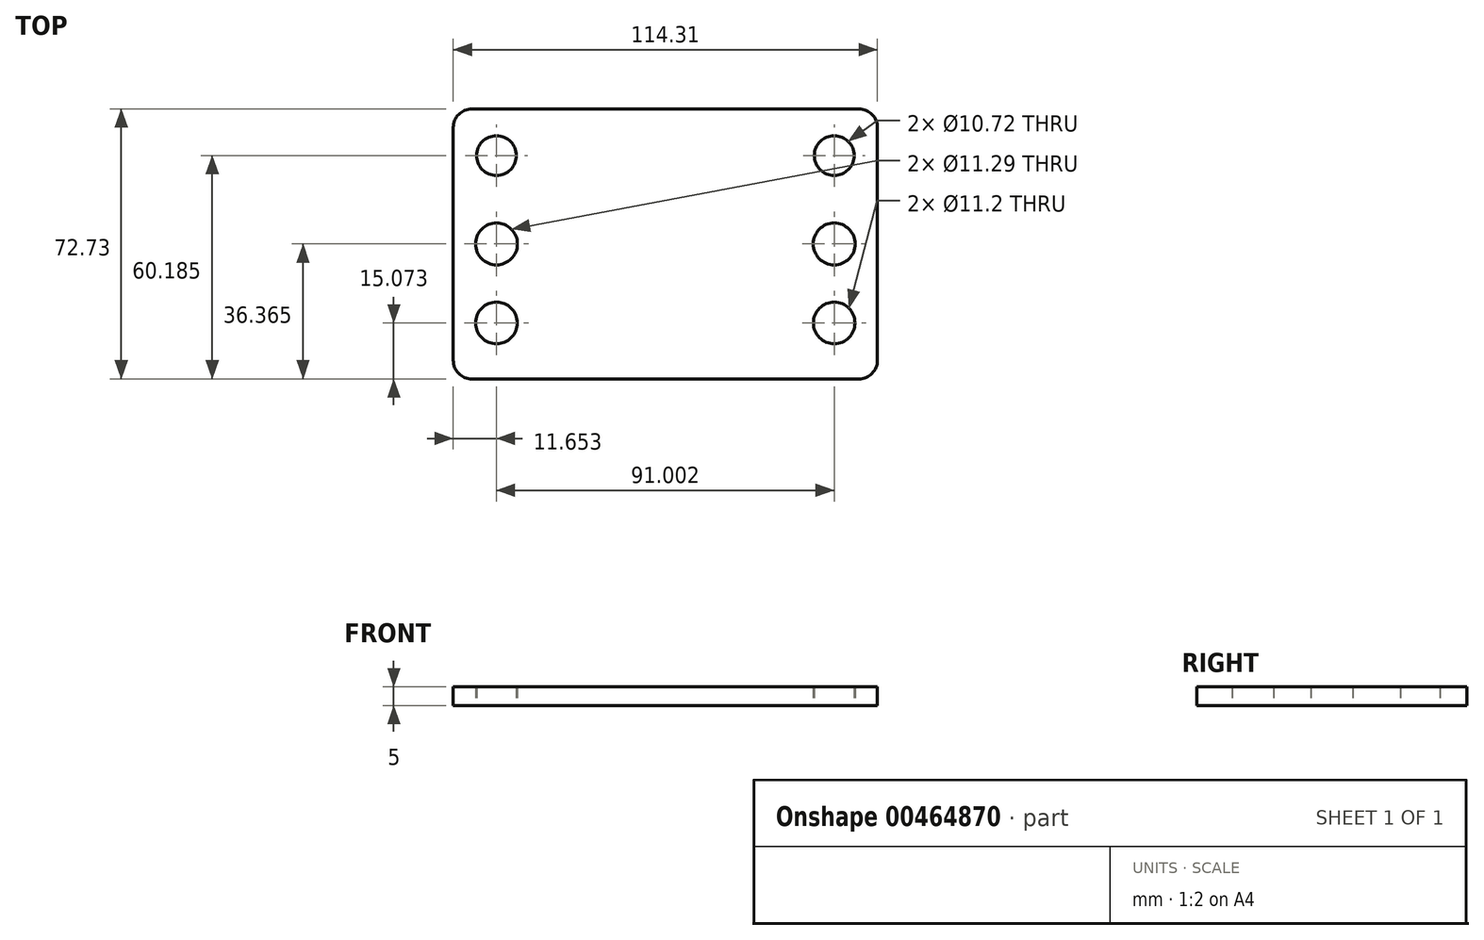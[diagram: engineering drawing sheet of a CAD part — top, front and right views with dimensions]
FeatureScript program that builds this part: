
annotation { "Feature Type Name" : "Feature", "Feature Type Description" : "" }
export const myFeature = defineFeature(function(context is Context, id is Id, definition is map)
    precondition{}
    {
        {
            var Q0;
            Q0=qCreatedBy(makeId("Top.planeOp"),FACE);
            var sketch = newSketch(context, id + "F0", { "sketchPlane" : qUnion([Q0])});
            skLineSegment(sketch, "E0.bottom", {"start": v(0, 0) * mm, "end": v(114.3, 0) * mm});
            skLineSegment(sketch, "E0.top", {"start": v(0, -72.73) * mm, "end": v(114.3, -72.73) * mm});
            skLineSegment(sketch, "E0.left", {"start": v(0, 0) * mm, "end": v(0, -72.73) * mm});
            skLineSegment(sketch, "E0.right", {"start": v(114.3, 0) * mm, "end": v(114.3, -72.73) * mm});
            skCircle(sketch, "E1", {"center": v(11.65, -36.36) * mm, "radius": 5.64 * mm});
            skPoint(sketch, "E1.centerSnap0", {"position": v(0, -36.36) * mm});
            skCircle(sketch, "E2", {"center": v(11.65, -57.66) * mm, "radius": 5.6 * mm});
            skCircle(sketch, "E3", {"center": v(11.65, -12.54) * mm, "radius": 5.36 * mm});
            skLineSegment(sketch, "E4", {"start": v(57.15, 0) * mm, "end": v(57.15, 9.99) * mm});
            skCircle(sketch, "E5.MirrorC", {"center": v(102.65, -36.36) * mm, "radius": 5.64 * mm});
            skCircle(sketch, "E6.MirrorC", {"center": v(102.65, -12.54) * mm, "radius": 5.36 * mm});
            skCircle(sketch, "E7.MirrorC", {"center": v(102.65, -57.66) * mm, "radius": 5.6 * mm});
            skSolve(sketch);
        }
        {
            var Q0;
            Q0 = qSketchRegion(id + "F0", true);
            extrude(context, id + "F1", {"entities" : qUnion([Q0]), "depth" : 5 * mm});
        }
        {
            var Q0;
            Q0=makeQuery(id+"F1.opExtrude","SWEPT_EDGE",EDGE,{"disambiguationData":[OSD([sQuery(id+"F0.wireOp",EDGE,"E0.bottom"),sQuery(id+"F0.wireOp",EDGE,"E0.right")])]});
            fillet(context, id + "F2", {"entities" : qUnion([Q0]), "radius" : 5 * mm, "tangentPropagation" : true, "allowEdgeOverflow" : false});
        }
        {
            var Q0;
            Q0=makeQuery(id+"F1.opExtrude","SWEPT_EDGE",EDGE,{"disambiguationData":[OSD([sQuery(id+"F0.wireOp",EDGE,"E0.bottom"),sQuery(id+"F0.wireOp",EDGE,"E0.left")])]});
            fillet(context, id + "F3", {"entities" : qUnion([Q0]), "radius" : 5 * mm, "tangentPropagation" : true, "allowEdgeOverflow" : false});
        }
        {
            var Q0;
            Q0=makeQuery(id+"F1.opExtrude","SWEPT_EDGE",EDGE,{"disambiguationData":[OSD([sQuery(id+"F0.wireOp",EDGE,"E0.top"),sQuery(id+"F0.wireOp",EDGE,"E0.right")])]});
            fillet(context, id + "F4", {"entities" : qUnion([Q0]), "radius" : 5 * mm, "tangentPropagation" : true, "allowEdgeOverflow" : false});
        }
        {
            var Q0;
            Q0=makeQuery(id+"F1.opExtrude","SWEPT_EDGE",EDGE,{"disambiguationData":[OSD([sQuery(id+"F0.wireOp",EDGE,"E0.top"),sQuery(id+"F0.wireOp",EDGE,"E0.left")])]});
            fillet(context, id + "F5", {"entities" : qUnion([Q0]), "radius" : 5 * mm, "tangentPropagation" : true, "allowEdgeOverflow" : false});
        }
    });
